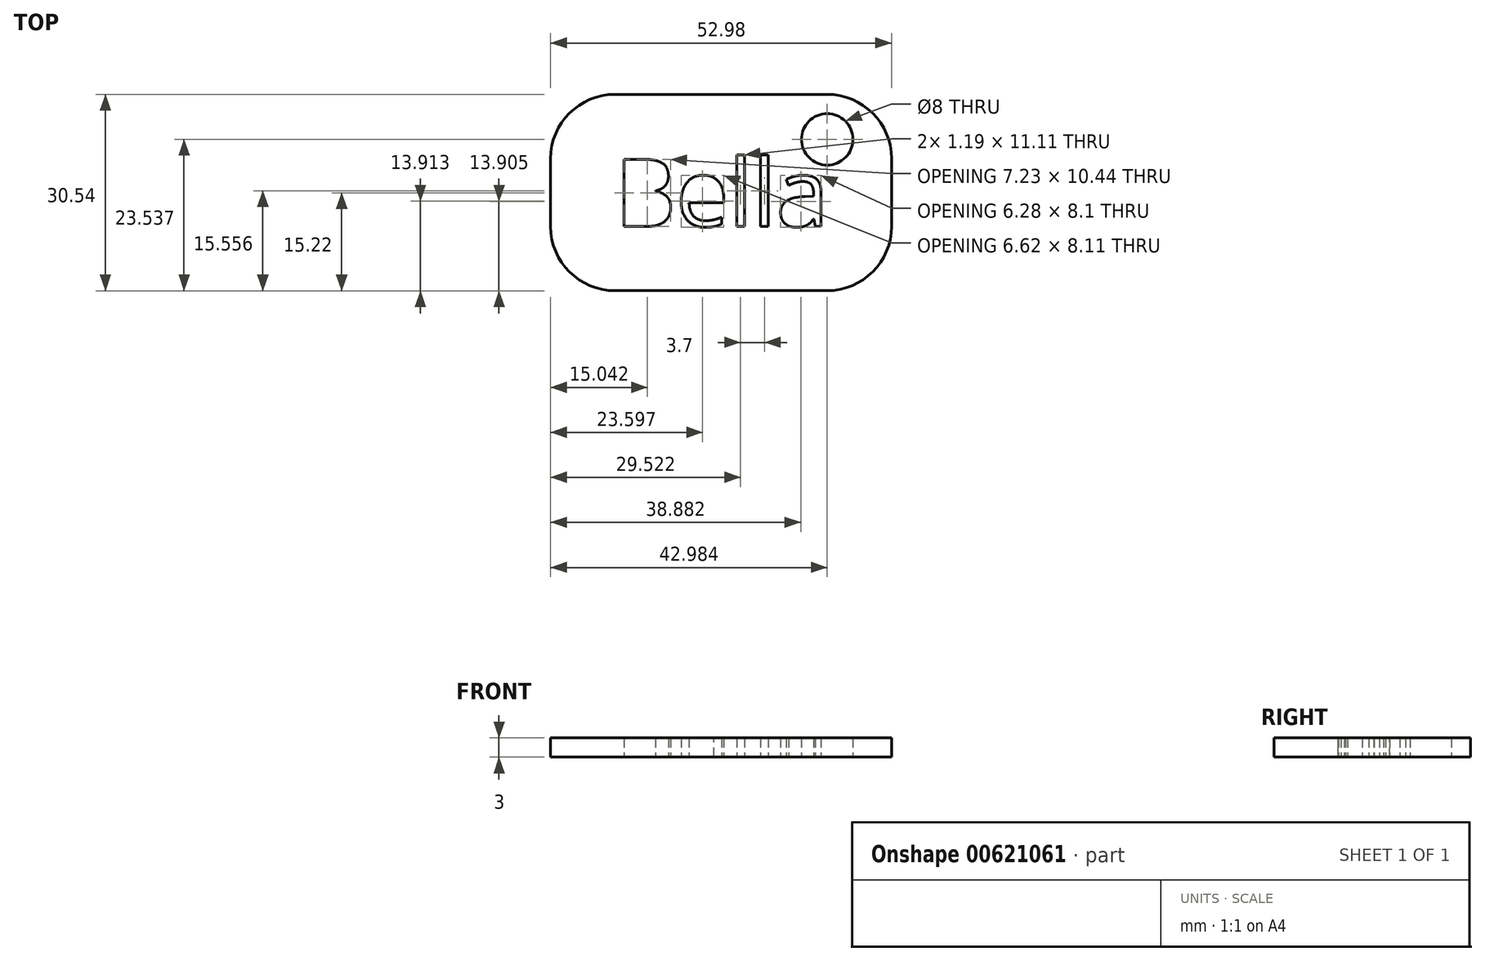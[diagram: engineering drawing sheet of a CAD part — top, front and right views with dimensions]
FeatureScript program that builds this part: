
annotation { "Feature Type Name" : "Feature", "Feature Type Description" : "" }
export const myFeature = defineFeature(function(context is Context, id is Id, definition is map)
    precondition{}
    {
        {
            var Q0;
            Q0=qCreatedBy(makeId("Top.planeOp"),FACE);
            var sketch = newSketch(context, id + "F0", { "sketchPlane" : qUnion([Q0])});
            skLineSegment(sketch, "E0.bottom", {"start": v(16.5, 15.27) * mm, "end": v(-16.5, 15.27) * mm});
            skLineSegment(sketch, "E0.top", {"start": v(16.5, -15.27) * mm, "end": v(-16.5, -15.27) * mm});
            skLineSegment(sketch, "E0.left", {"start": v(26.5, 5.27) * mm, "end": v(26.5, -5.27) * mm});
            skLineSegment(sketch, "E0.right", {"start": v(-26.5, 5.27) * mm, "end": v(-26.5, -5.27) * mm});
            skPoint(sketch, "E0.middle", {"position": v(0, 0) * mm});
            skPoint(sketch, "E1.visualSharp", {"position": v(26.5, 15.27) * mm});
            skArc(sketch, "E1.filletArc", {"start": v(26.5, 5.27) * mm, "mid": v(23.57, 12.34) * mm, "end": v(16.5, 15.27) * mm});
            skPoint(sketch, "E2.visualSharp", {"position": v(26.5, -15.27) * mm});
            skArc(sketch, "E2.filletArc", {"start": v(16.5, -15.27) * mm, "mid": v(23.57, -12.34) * mm, "end": v(26.5, -5.27) * mm});
            skPoint(sketch, "E3.visualSharp", {"position": v(-26.5, -15.27) * mm});
            skArc(sketch, "E3.filletArc", {"start": v(-26.5, -5.27) * mm, "mid": v(-23.57, -12.34) * mm, "end": v(-16.5, -15.27) * mm});
            skPoint(sketch, "E4.visualSharp", {"position": v(-26.5, 15.27) * mm});
            skArc(sketch, "E4.filletArc", {"start": v(-16.5, 15.27) * mm, "mid": v(-23.57, 12.34) * mm, "end": v(-26.5, 5.27) * mm});
            skText(sketch, "E5", { "text": "Bella\n", "fontName": "OpenSans-Regular.ttf"});
            skCircle(sketch, "E6", {"center": v(16.5, 8.27) * mm, "radius": 4 * mm});
            const initialGuessF0  = {"E5": [-0.0165, -0.00527, 1, 0, 0.01053]};
            skSetInitialGuess(sketch, initialGuessF0);
            skSolve(sketch);
        }
        {
            var Q0;
            Q0=makeQuery(id+"F0.imprint","IMPRINT",FACE,{"disambiguationData":[TD([[makeQuery(id+"F0.imprint","IMPRINT",EDGE,{"derivedFrom":sQuery(id+"F0.wireOp",EDGE,"E0.bottom")}),1.0]])]});
            extrude(context, id + "F1", {"entities" : qUnion([Q0]), "depth" : 3 * mm, "offsetDistance" : 25 * mm});
        }
    });
